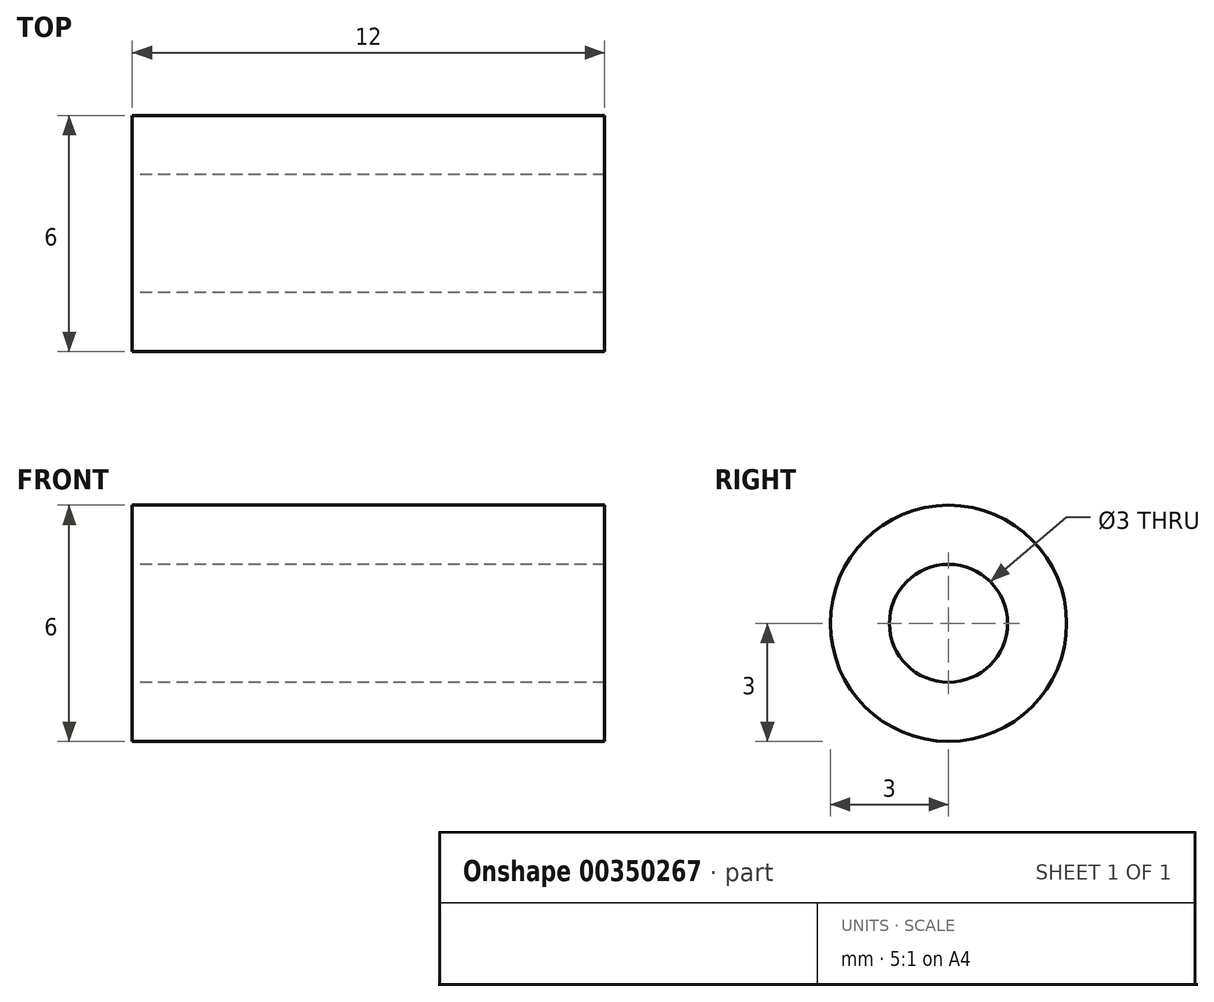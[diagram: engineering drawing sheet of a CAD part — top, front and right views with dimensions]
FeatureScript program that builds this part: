
annotation { "Feature Type Name" : "Feature", "Feature Type Description" : "" }
export const myFeature = defineFeature(function(context is Context, id is Id, definition is map)
    precondition{}
    {
        {
            var Q0;
            Q0=qCreatedBy(makeId("Right.planeOp"),FACE);
            var sketch = newSketch(context, id + "F0", { "sketchPlane" : qUnion([Q0])});
            skCircle(sketch, "E0", {"center": v(0, 0) * mm, "radius": 3 * mm});
            skCircle(sketch, "E1", {"center": v(0, 0) * mm, "radius": 1.5 * mm});
            skSolve(sketch);
        }
        {
            var Q0;
            Q0=makeQuery(id+"F0.imprint","IMPRINT",FACE,{"disambiguationData":[TD([[makeQuery(id+"F0.imprint","IMPRINT",EDGE,{"derivedFrom":sQuery(id+"F0.wireOp",EDGE,"E0")}),1.0]])]});
            extrude(context, id + "F1", {"entities" : qUnion([Q0]), "depth" : 12 * mm});
        }
    });
